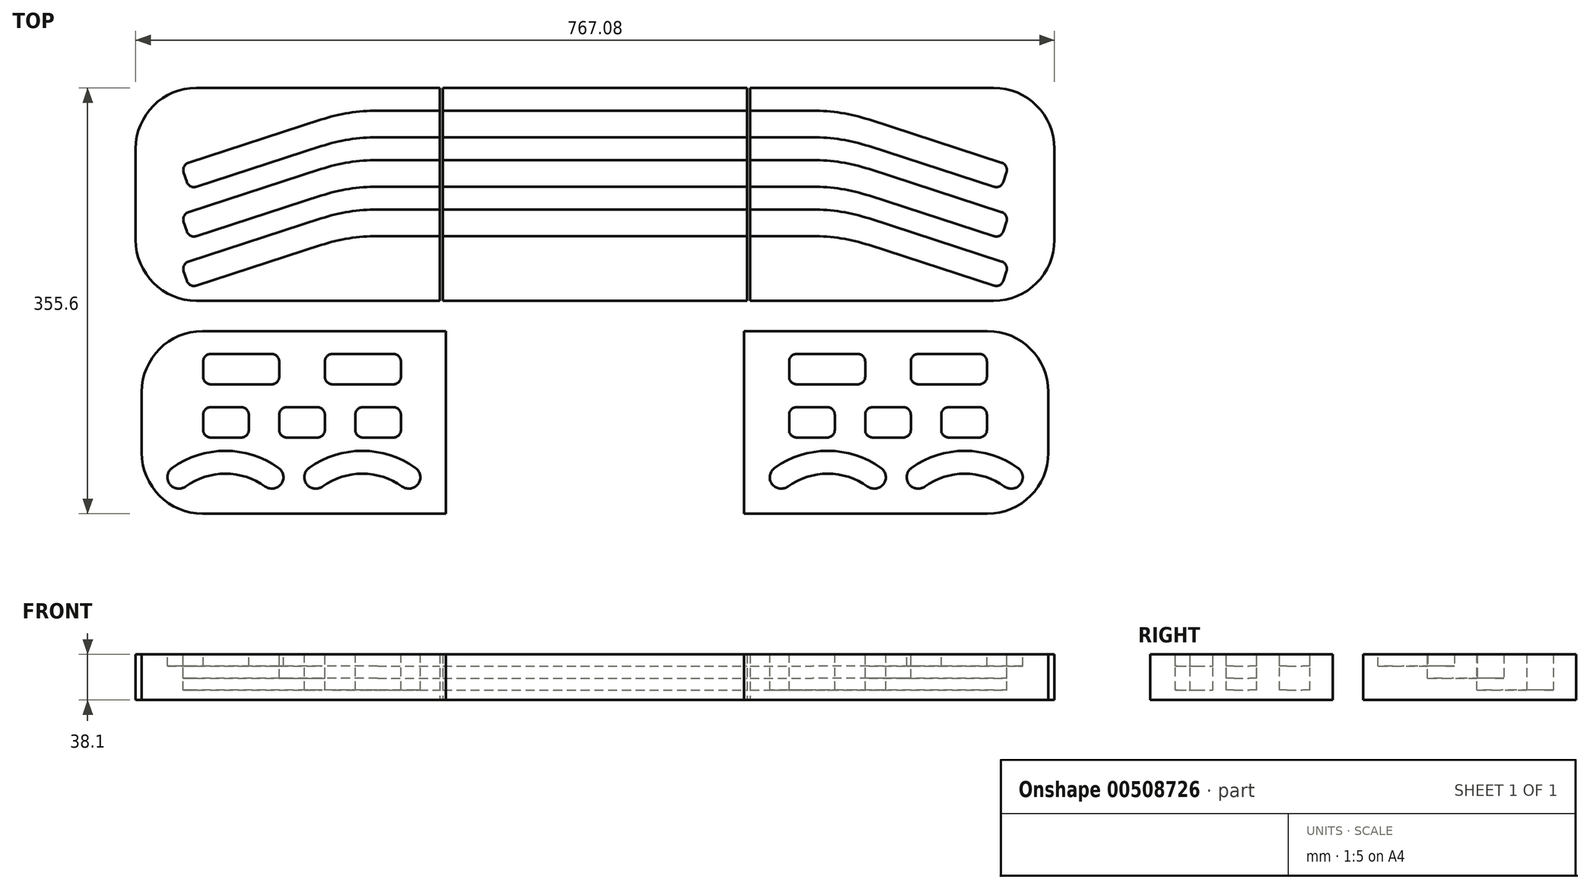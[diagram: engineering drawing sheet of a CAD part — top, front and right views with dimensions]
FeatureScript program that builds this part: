
annotation { "Feature Type Name" : "Feature", "Feature Type Description" : "" }
export const myFeature = defineFeature(function(context is Context, id is Id, definition is map)
    precondition{}
    {
        {
            var Q0;
            Q0=qCreatedBy(makeId("Top.planeOp"),FACE);
            var sketch = newSketch(context, id + "F0", { "sketchPlane" : qUnion([Q0])});
            skLineSegment(sketch, "E0.bottom", {"start": v(-716.28, 177.8) * mm, "end": v(-513.08, 177.8) * mm});
            skLineSegment(sketch, "E0.top", {"start": v(-716.28, 0) * mm, "end": v(-513.08, 0) * mm});
            skLineSegment(sketch, "E0.left", {"start": v(-767.08, 127) * mm, "end": v(-767.08, 50.8) * mm});
            skLineSegment(sketch, "E0.right", {"start": v(0, 127) * mm, "end": v(0, 50.8) * mm});
            skPoint(sketch, "E1.visualSharp", {"position": v(-767.08, 177.8) * mm});
            skArc(sketch, "E1.filletArc", {"start": v(-716.28, 177.8) * mm, "mid": v(-752.2, 162.92) * mm, "end": v(-767.08, 127) * mm});
            skPoint(sketch, "E2.visualSharp", {"position": v(0, 177.8) * mm});
            skArc(sketch, "E2.filletArc", {"start": v(0, 127) * mm, "mid": v(-14.88, 162.92) * mm, "end": v(-50.8, 177.8) * mm});
            skPoint(sketch, "E3.visualSharp", {"position": v(0, 0) * mm});
            skArc(sketch, "E3.filletArc", {"start": v(-50.8, 0) * mm, "mid": v(-14.88, 14.88) * mm, "end": v(0, 50.8) * mm});
            skPoint(sketch, "E4.visualSharp", {"position": v(-767.08, 0) * mm});
            skArc(sketch, "E4.filletArc", {"start": v(-767.08, 50.8) * mm, "mid": v(-752.2, 14.88) * mm, "end": v(-716.28, 0) * mm});
            skLineSegment(sketch, "E5", {"start": v(-513.08, 177.8) * mm, "end": v(-513.08, 0) * mm});
            skLineSegment(sketch, "E6", {"start": v(-254, 177.8) * mm, "end": v(-254, 0) * mm});
            skLineSegment(sketch, "E7", {"start": v(-510.54, 177.8) * mm, "end": v(-510.54, 0) * mm});
            skLineSegment(sketch, "E8", {"start": v(-256.54, 177.8) * mm, "end": v(-256.54, 0) * mm});
            skLineSegment(sketch, "E9.trimOffspring", {"start": v(-254, 177.8) * mm, "end": v(-50.8, 177.8) * mm});
            skLineSegment(sketch, "E10.trimOffspring", {"start": v(-254, 0) * mm, "end": v(-50.8, 0) * mm});
            skLineSegment(sketch, "E11.trimOffspring", {"start": v(-510.54, 177.8) * mm, "end": v(-256.54, 177.8) * mm});
            skLineSegment(sketch, "E12.trimOffspring", {"start": v(-510.54, 0) * mm, "end": v(-256.54, 0) * mm});
            skSolve(sketch);
        }
        {
            var Q0;
            Q0=makeQuery(id+"F0.imprint","IMPRINT",FACE,{"disambiguationData":[TD([[makeQuery(id+"F0.imprint","IMPRINT",EDGE,{"derivedFrom":sQuery(id+"F0.wireOp",EDGE,"E0.left")}),1.0]])]});
            var Q1;
            Q1=makeQuery(id+"F0.imprint","IMPRINT",FACE,{"disambiguationData":[TD([[makeQuery(id+"F0.imprint","IMPRINT",EDGE,{"derivedFrom":sQuery(id+"F0.wireOp",EDGE,"E0.right")}),-1.0]])]});
            var Q2;
            {var subQ0=sQuery(id+"F0.wireOp",EDGE,"E5");Q2=makeQuery(id+"F0.imprint","IMPRINT",FACE,{"disambiguationData":[TD([[makeQuery(id+"F0.imprint","IMPRINT",EDGE,{"derivedFrom":subQ0}),1.0]])]});}
            var Q3;
            Q3=makeQuery(id+"F0.imprint","IMPRINT",FACE,{"disambiguationData":[TD([[makeQuery(id+"F0.imprint","IMPRINT",EDGE,{"derivedFrom":sQuery(id+"F0.wireOp",EDGE,"E7")}),1.0]])]});
            extrude(context, id + "F1", {"entities" : qUnion([Q0, Q1, Q2, Q3]), "depth" : 38.1 * mm});
        }
        {
            var Q0;
            Q0=makeQuery(id+"F1.opExtrude","CAP_FACE",FACE,{"disambiguationData":[OSD([sQuery(id+"F0.wireOp",EDGE,"E0.bottom"),sQuery(id+"F0.wireOp",EDGE,"E0.top"),sQuery(id+"F0.wireOp",EDGE,"E0.left"),sQuery(id+"F0.wireOp",EDGE,"E0.right"),sQuery(id+"F0.wireOp",EDGE,"E1.filletArc"),sQuery(id+"F0.wireOp",EDGE,"E2.filletArc"),sQuery(id+"F0.wireOp",EDGE,"E3.filletArc"),sQuery(id+"F0.wireOp",EDGE,"E4.filletArc")])],"isStart":false});
            var sketch = newSketch(context, id + "F2", { "sketchPlane" : qUnion([Q0])});
            skLineSegment(sketch, "E13.bottom", {"start": v(-565.14, 158.75) * mm, "end": v(-201.94, 158.75) * mm});
            skLineSegment(sketch, "E13.top", {"start": v(-565.14, 136.53) * mm, "end": v(-201.94, 136.53) * mm});
            skLineSegment(sketch, "E14", {"start": v(-612.24, 151.3) * mm, "end": v(-722.94, 115.32) * mm});
            skLineSegment(sketch, "E15", {"start": v(-727.02, 107.32) * mm, "end": v(-724.41, 99.3) * mm});
            skLineSegment(sketch, "E16", {"start": v(-716.4, 95.22) * mm, "end": v(-612.24, 129.07) * mm});
            skLineSegment(sketch, "E17", {"start": v(-154.84, 151.3) * mm, "end": v(-44.14, 115.32) * mm});
            skLineSegment(sketch, "E18", {"start": v(-40.06, 107.32) * mm, "end": v(-42.67, 99.3) * mm});
            skLineSegment(sketch, "E19", {"start": v(-50.67, 95.22) * mm, "end": v(-154.84, 129.07) * mm});
            skPoint(sketch, "E20.visualSharp", {"position": v(-589.28, 158.75) * mm});
            skArc(sketch, "E20.filletArc", {"start": v(-565.14, 158.75) * mm, "mid": v(-588.98, 156.87) * mm, "end": v(-612.24, 151.3) * mm});
            skPoint(sketch, "E21.visualSharp", {"position": v(-589.28, 136.53) * mm});
            skArc(sketch, "E21.filletArc", {"start": v(-565.14, 136.53) * mm, "mid": v(-588.98, 134.65) * mm, "end": v(-612.24, 129.07) * mm});
            skPoint(sketch, "E22.visualSharp", {"position": v(-177.8, 158.75) * mm});
            skArc(sketch, "E22.filletArc", {"start": v(-154.84, 151.3) * mm, "mid": v(-178.1, 156.87) * mm, "end": v(-201.94, 158.75) * mm});
            skPoint(sketch, "E23.visualSharp", {"position": v(-177.8, 136.53) * mm});
            skArc(sketch, "E23.filletArc", {"start": v(-154.84, 129.07) * mm, "mid": v(-178.1, 134.65) * mm, "end": v(-201.94, 136.53) * mm});
            skPoint(sketch, "E24.visualSharp", {"position": v(-38.1, 113.36) * mm});
            skArc(sketch, "E24.filletArc", {"start": v(-40.06, 107.32) * mm, "mid": v(-40.44, 112.16) * mm, "end": v(-44.14, 115.32) * mm});
            skPoint(sketch, "E25.visualSharp", {"position": v(-44.63, 93.26) * mm});
            skArc(sketch, "E25.filletArc", {"start": v(-50.67, 95.22) * mm, "mid": v(-45.83, 95.6) * mm, "end": v(-42.67, 99.3) * mm});
            skPoint(sketch, "E26.visualSharp", {"position": v(-728.98, 113.36) * mm});
            skArc(sketch, "E26.filletArc", {"start": v(-722.94, 115.32) * mm, "mid": v(-726.64, 112.16) * mm, "end": v(-727.02, 107.32) * mm});
            skPoint(sketch, "E27.visualSharp", {"position": v(-722.45, 93.26) * mm});
            skArc(sketch, "E27.filletArc", {"start": v(-724.41, 99.3) * mm, "mid": v(-721.25, 95.6) * mm, "end": v(-716.4, 95.22) * mm});
            skLineSegment(sketch, "E28.bottom", {"start": v(-565.14, 117.47) * mm, "end": v(-201.94, 117.47) * mm});
            skLineSegment(sketch, "E28.top", {"start": v(-565.14, 95.25) * mm, "end": v(-201.94, 95.25) * mm});
            skLineSegment(sketch, "E29", {"start": v(-612.24, 110.02) * mm, "end": v(-722.94, 74.05) * mm});
            skLineSegment(sketch, "E30", {"start": v(-727.02, 66.04) * mm, "end": v(-724.41, 58.02) * mm});
            skLineSegment(sketch, "E31", {"start": v(-716.4, 53.94) * mm, "end": v(-612.24, 87.8) * mm});
            skLineSegment(sketch, "E32", {"start": v(-154.84, 110.02) * mm, "end": v(-44.14, 74.05) * mm});
            skLineSegment(sketch, "E33", {"start": v(-40.06, 66.04) * mm, "end": v(-42.67, 58.02) * mm});
            skLineSegment(sketch, "E34", {"start": v(-50.67, 53.94) * mm, "end": v(-154.84, 87.8) * mm});
            skPoint(sketch, "E35.visualSharp", {"position": v(-589.28, 117.48) * mm});
            skArc(sketch, "E35.filletArc", {"start": v(-565.14, 117.48) * mm, "mid": v(-588.98, 115.6) * mm, "end": v(-612.24, 110.02) * mm});
            skPoint(sketch, "E36.visualSharp", {"position": v(-589.28, 95.25) * mm});
            skArc(sketch, "E36.filletArc", {"start": v(-565.14, 95.25) * mm, "mid": v(-588.98, 93.37) * mm, "end": v(-612.24, 87.8) * mm});
            skPoint(sketch, "E37.visualSharp", {"position": v(-177.8, 117.48) * mm});
            skArc(sketch, "E37.filletArc", {"start": v(-154.84, 110.02) * mm, "mid": v(-178.1, 115.6) * mm, "end": v(-201.94, 117.48) * mm});
            skPoint(sketch, "E38.visualSharp", {"position": v(-177.8, 95.25) * mm});
            skArc(sketch, "E38.filletArc", {"start": v(-154.84, 87.8) * mm, "mid": v(-178.1, 93.37) * mm, "end": v(-201.94, 95.25) * mm});
            skPoint(sketch, "E39.visualSharp", {"position": v(-38.1, 72.08) * mm});
            skArc(sketch, "E39.filletArc", {"start": v(-40.06, 66.04) * mm, "mid": v(-40.44, 70.89) * mm, "end": v(-44.14, 74.05) * mm});
            skPoint(sketch, "E40.visualSharp", {"position": v(-44.63, 51.98) * mm});
            skArc(sketch, "E40.filletArc", {"start": v(-50.67, 53.94) * mm, "mid": v(-45.83, 54.32) * mm, "end": v(-42.67, 58.02) * mm});
            skPoint(sketch, "E41.visualSharp", {"position": v(-728.98, 72.08) * mm});
            skArc(sketch, "E41.filletArc", {"start": v(-722.94, 74.05) * mm, "mid": v(-726.64, 70.89) * mm, "end": v(-727.02, 66.04) * mm});
            skPoint(sketch, "E42.visualSharp", {"position": v(-722.45, 51.98) * mm});
            skArc(sketch, "E42.filletArc", {"start": v(-724.41, 58.02) * mm, "mid": v(-721.25, 54.32) * mm, "end": v(-716.4, 53.94) * mm});
            skLineSegment(sketch, "E43.bottom", {"start": v(-565.14, 76.2) * mm, "end": v(-201.94, 76.2) * mm});
            skLineSegment(sketch, "E43.top", {"start": v(-565.14, 53.97) * mm, "end": v(-201.94, 53.97) * mm});
            skLineSegment(sketch, "E44", {"start": v(-612.24, 68.74) * mm, "end": v(-722.94, 32.77) * mm});
            skLineSegment(sketch, "E45", {"start": v(-727.02, 24.77) * mm, "end": v(-724.41, 16.75) * mm});
            skLineSegment(sketch, "E46", {"start": v(-716.4, 12.67) * mm, "end": v(-612.24, 46.52) * mm});
            skLineSegment(sketch, "E47", {"start": v(-154.84, 68.74) * mm, "end": v(-44.14, 32.77) * mm});
            skLineSegment(sketch, "E48", {"start": v(-40.06, 24.77) * mm, "end": v(-42.67, 16.75) * mm});
            skLineSegment(sketch, "E49", {"start": v(-50.67, 12.67) * mm, "end": v(-154.84, 46.52) * mm});
            skPoint(sketch, "E50.visualSharp", {"position": v(-589.28, 76.2) * mm});
            skArc(sketch, "E50.filletArc", {"start": v(-565.14, 76.2) * mm, "mid": v(-588.98, 74.32) * mm, "end": v(-612.24, 68.74) * mm});
            skPoint(sketch, "E51.visualSharp", {"position": v(-589.28, 53.98) * mm});
            skArc(sketch, "E51.filletArc", {"start": v(-565.14, 53.98) * mm, "mid": v(-588.98, 52.1) * mm, "end": v(-612.24, 46.52) * mm});
            skPoint(sketch, "E52.visualSharp", {"position": v(-177.8, 76.2) * mm});
            skArc(sketch, "E52.filletArc", {"start": v(-154.84, 68.74) * mm, "mid": v(-178.1, 74.32) * mm, "end": v(-201.94, 76.2) * mm});
            skPoint(sketch, "E53.visualSharp", {"position": v(-177.8, 53.97) * mm});
            skArc(sketch, "E53.filletArc", {"start": v(-154.84, 46.52) * mm, "mid": v(-178.1, 52.1) * mm, "end": v(-201.94, 53.98) * mm});
            skPoint(sketch, "E54.visualSharp", {"position": v(-38.1, 30.8) * mm});
            skArc(sketch, "E54.filletArc", {"start": v(-40.06, 24.77) * mm, "mid": v(-40.44, 29.61) * mm, "end": v(-44.14, 32.77) * mm});
            skPoint(sketch, "E55.visualSharp", {"position": v(-44.63, 10.7) * mm});
            skArc(sketch, "E55.filletArc", {"start": v(-50.67, 12.67) * mm, "mid": v(-45.83, 13.05) * mm, "end": v(-42.67, 16.75) * mm});
            skPoint(sketch, "E56.visualSharp", {"position": v(-728.98, 30.8) * mm});
            skArc(sketch, "E56.filletArc", {"start": v(-722.94, 32.77) * mm, "mid": v(-726.64, 29.61) * mm, "end": v(-727.02, 24.77) * mm});
            skPoint(sketch, "E57.visualSharp", {"position": v(-722.45, 10.7) * mm});
            skArc(sketch, "E57.filletArc", {"start": v(-724.41, 16.75) * mm, "mid": v(-721.25, 13.05) * mm, "end": v(-716.4, 12.67) * mm});
            skLineSegment(sketch, "E58", {"start": v(-614.68, 177.8) * mm, "end": v(-614.68, 0) * mm, "construction": true});
            skSolve(sketch);
        }
        {
            var Q0;
            Q0=qCreatedBy(makeId("Top.planeOp"),FACE);
            var sketch = newSketch(context, id + "F3", { "sketchPlane" : qUnion([Q0])});
            skLineSegment(sketch, "E59.bottom", {"start": v(-711.2, -25.4) * mm, "end": v(-508, -25.4) * mm});
            skLineSegment(sketch, "E59.top", {"start": v(-711.2, -177.8) * mm, "end": v(-508, -177.8) * mm});
            skLineSegment(sketch, "E59.left", {"start": v(-762, -76.2) * mm, "end": v(-762, -127) * mm});
            skPoint(sketch, "E60.visualSharp", {"position": v(-762, -25.4) * mm});
            skArc(sketch, "E60.filletArc", {"start": v(-711.2, -25.4) * mm, "mid": v(-747.12, -40.28) * mm, "end": v(-762, -76.2) * mm});
            skPoint(sketch, "E61.visualSharp", {"position": v(0, -25.4) * mm});
            skPoint(sketch, "E62.visualSharp", {"position": v(0, -177.8) * mm});
            skPoint(sketch, "E63.visualSharp", {"position": v(-762, -177.8) * mm});
            skArc(sketch, "E63.filletArc", {"start": v(-762, -127) * mm, "mid": v(-747.12, -162.92) * mm, "end": v(-711.2, -177.8) * mm});
            skLineSegment(sketch, "E64", {"start": v(-508, -25.4) * mm, "end": v(-508, -177.8) * mm});
            skSolve(sketch);
        }
        {
            var Q0;
            Q0=makeQuery(id+"F3.imprint","IMPRINT",FACE,{"disambiguationData":[TD([[makeQuery(id+"F3.imprint","IMPRINT",EDGE,{"derivedFrom":sQuery(id+"F3.wireOp",EDGE,"E59.bottom")}),-1.0]])]});
            extrude(context, id + "F4", {"entities" : qUnion([Q0]), "depth" : 38.1 * mm});
        }
        {
            var Q0;
            Q0=makeQuery(id+"F4.opExtrude","CAP_FACE",FACE,{"disambiguationData":[OSD([sQuery(id+"F3.wireOp",EDGE,"E59.bottom"),sQuery(id+"F3.wireOp",EDGE,"E59.top"),sQuery(id+"F3.wireOp",EDGE,"E59.left"),sQuery(id+"F3.wireOp",EDGE,"E59.right"),sQuery(id+"F3.wireOp",EDGE,"E60.filletArc"),sQuery(id+"F3.wireOp",EDGE,"E61.filletArc"),sQuery(id+"F3.wireOp",EDGE,"E62.filletArc"),sQuery(id+"F3.wireOp",EDGE,"E63.filletArc")])],"isStart":false});
            var sketch = newSketch(context, id + "F5", { "sketchPlane" : qUnion([Q0])});
            skLineSegment(sketch, "E65.bottom", {"start": v(-704.32, -69.85) * mm, "end": v(-653.52, -69.85) * mm});
            skLineSegment(sketch, "E65.top", {"start": v(-704.32, -44.45) * mm, "end": v(-653.52, -44.45) * mm});
            skLineSegment(sketch, "E65.left", {"start": v(-710.67, -63.5) * mm, "end": v(-710.67, -50.8) * mm});
            skLineSegment(sketch, "E65.right", {"start": v(-647.17, -63.5) * mm, "end": v(-647.17, -50.8) * mm});
            skPoint(sketch, "E66.visualSharp", {"position": v(-710.67, -44.45) * mm});
            skArc(sketch, "E66.filletArc", {"start": v(-704.32, -44.45) * mm, "mid": v(-708.81, -46.3) * mm, "end": v(-710.67, -50.8) * mm});
            skPoint(sketch, "E67.visualSharp", {"position": v(-710.67, -69.85) * mm});
            skArc(sketch, "E67.filletArc", {"start": v(-710.67, -63.5) * mm, "mid": v(-708.81, -68) * mm, "end": v(-704.32, -69.85) * mm});
            skPoint(sketch, "E68.visualSharp", {"position": v(-647.17, -44.45) * mm});
            skArc(sketch, "E68.filletArc", {"start": v(-647.17, -50.8) * mm, "mid": v(-649.03, -46.3) * mm, "end": v(-653.52, -44.45) * mm});
            skPoint(sketch, "E69.visualSharp", {"position": v(-647.17, -69.85) * mm});
            skArc(sketch, "E69.filletArc", {"start": v(-653.52, -69.85) * mm, "mid": v(-649.03, -68) * mm, "end": v(-647.17, -63.5) * mm});
            skLineSegment(sketch, "E70.bottom", {"start": v(-602.72, -69.85) * mm, "end": v(-551.92, -69.85) * mm});
            skLineSegment(sketch, "E70.top", {"start": v(-602.72, -44.45) * mm, "end": v(-551.92, -44.45) * mm});
            skLineSegment(sketch, "E70.left", {"start": v(-609.07, -63.5) * mm, "end": v(-609.07, -50.8) * mm});
            skLineSegment(sketch, "E70.right", {"start": v(-545.57, -63.5) * mm, "end": v(-545.57, -50.8) * mm});
            skPoint(sketch, "E71.visualSharp", {"position": v(-609.07, -44.45) * mm});
            skArc(sketch, "E71.filletArc", {"start": v(-602.72, -44.45) * mm, "mid": v(-607.21, -46.3) * mm, "end": v(-609.07, -50.8) * mm});
            skPoint(sketch, "E72.visualSharp", {"position": v(-609.07, -69.85) * mm});
            skArc(sketch, "E72.filletArc", {"start": v(-609.07, -63.5) * mm, "mid": v(-607.21, -68) * mm, "end": v(-602.72, -69.85) * mm});
            skPoint(sketch, "E73.visualSharp", {"position": v(-545.57, -44.45) * mm});
            skArc(sketch, "E73.filletArc", {"start": v(-545.57, -50.8) * mm, "mid": v(-547.43, -46.3) * mm, "end": v(-551.92, -44.45) * mm});
            skPoint(sketch, "E74.visualSharp", {"position": v(-545.57, -69.85) * mm});
            skArc(sketch, "E74.filletArc", {"start": v(-551.92, -69.85) * mm, "mid": v(-547.43, -68) * mm, "end": v(-545.57, -63.5) * mm});
            skLineSegment(sketch, "E75.bottom", {"start": v(-704.32, -114.3) * mm, "end": v(-678.92, -114.3) * mm});
            skLineSegment(sketch, "E75.top", {"start": v(-704.32, -88.9) * mm, "end": v(-678.92, -88.9) * mm});
            skLineSegment(sketch, "E75.left", {"start": v(-710.67, -107.95) * mm, "end": v(-710.67, -95.25) * mm});
            skLineSegment(sketch, "E75.right", {"start": v(-672.57, -107.95) * mm, "end": v(-672.57, -95.25) * mm});
            skPoint(sketch, "E76.visualSharp", {"position": v(-710.67, -88.9) * mm});
            skArc(sketch, "E76.filletArc", {"start": v(-704.32, -88.9) * mm, "mid": v(-708.81, -90.76) * mm, "end": v(-710.67, -95.25) * mm});
            skPoint(sketch, "E77.visualSharp", {"position": v(-710.67, -114.3) * mm});
            skArc(sketch, "E77.filletArc", {"start": v(-710.67, -107.95) * mm, "mid": v(-708.81, -112.44) * mm, "end": v(-704.32, -114.3) * mm});
            skPoint(sketch, "E78.visualSharp", {"position": v(-672.57, -88.9) * mm});
            skArc(sketch, "E78.filletArc", {"start": v(-672.57, -95.25) * mm, "mid": v(-674.43, -90.76) * mm, "end": v(-678.92, -88.9) * mm});
            skPoint(sketch, "E79.visualSharp", {"position": v(-672.57, -114.3) * mm});
            skArc(sketch, "E79.filletArc", {"start": v(-678.92, -114.3) * mm, "mid": v(-674.43, -112.44) * mm, "end": v(-672.57, -107.95) * mm});
            skLineSegment(sketch, "E80.bottom", {"start": v(-640.82, -114.3) * mm, "end": v(-615.42, -114.3) * mm});
            skLineSegment(sketch, "E80.top", {"start": v(-640.82, -88.9) * mm, "end": v(-615.42, -88.9) * mm});
            skLineSegment(sketch, "E80.left", {"start": v(-647.17, -107.95) * mm, "end": v(-647.17, -95.25) * mm});
            skLineSegment(sketch, "E80.right", {"start": v(-609.07, -107.95) * mm, "end": v(-609.07, -95.25) * mm});
            skPoint(sketch, "E81.visualSharp", {"position": v(-647.17, -88.9) * mm});
            skArc(sketch, "E81.filletArc", {"start": v(-640.82, -88.9) * mm, "mid": v(-645.31, -90.76) * mm, "end": v(-647.17, -95.25) * mm});
            skPoint(sketch, "E82.visualSharp", {"position": v(-647.17, -114.3) * mm});
            skArc(sketch, "E82.filletArc", {"start": v(-647.17, -107.95) * mm, "mid": v(-645.31, -112.44) * mm, "end": v(-640.82, -114.3) * mm});
            skPoint(sketch, "E83.visualSharp", {"position": v(-609.07, -88.9) * mm});
            skArc(sketch, "E83.filletArc", {"start": v(-609.07, -95.25) * mm, "mid": v(-610.93, -90.76) * mm, "end": v(-615.42, -88.9) * mm});
            skPoint(sketch, "E84.visualSharp", {"position": v(-609.07, -114.3) * mm});
            skArc(sketch, "E84.filletArc", {"start": v(-615.42, -114.3) * mm, "mid": v(-610.93, -112.44) * mm, "end": v(-609.07, -107.95) * mm});
            skLineSegment(sketch, "E85.bottom", {"start": v(-577.32, -114.3) * mm, "end": v(-551.92, -114.3) * mm});
            skLineSegment(sketch, "E85.top", {"start": v(-577.32, -88.9) * mm, "end": v(-551.92, -88.9) * mm});
            skLineSegment(sketch, "E85.left", {"start": v(-583.67, -107.95) * mm, "end": v(-583.67, -95.25) * mm});
            skLineSegment(sketch, "E85.right", {"start": v(-545.57, -107.95) * mm, "end": v(-545.57, -95.25) * mm});
            skPoint(sketch, "E86.visualSharp", {"position": v(-583.67, -88.9) * mm});
            skArc(sketch, "E86.filletArc", {"start": v(-577.32, -88.9) * mm, "mid": v(-581.81, -90.76) * mm, "end": v(-583.67, -95.25) * mm});
            skPoint(sketch, "E87.visualSharp", {"position": v(-583.67, -114.3) * mm});
            skArc(sketch, "E87.filletArc", {"start": v(-583.67, -107.95) * mm, "mid": v(-581.81, -112.44) * mm, "end": v(-577.32, -114.3) * mm});
            skPoint(sketch, "E88.visualSharp", {"position": v(-545.57, -88.9) * mm});
            skArc(sketch, "E88.filletArc", {"start": v(-545.57, -95.25) * mm, "mid": v(-547.43, -90.76) * mm, "end": v(-551.92, -88.9) * mm});
            skPoint(sketch, "E89.visualSharp", {"position": v(-545.57, -114.3) * mm});
            skArc(sketch, "E89.filletArc", {"start": v(-551.92, -114.3) * mm, "mid": v(-547.43, -112.44) * mm, "end": v(-545.57, -107.95) * mm});
            skLineSegment(sketch, "E90", {"start": v(-736.6, -139.7) * mm, "end": v(-647.7, -139.7) * mm, "construction": true});
            skArc(sketch, "E91", {"start": v(-647.7, -139.7) * mm, "mid": v(-692.15, -125.4) * mm, "end": v(-736.6, -139.7) * mm});
            skArc(sketch, "E92.0", {"start": v(-658.81, -155.17) * mm, "mid": v(-692.15, -144.44) * mm, "end": v(-725.49, -155.17) * mm});
            skArc(sketch, "E93", {"start": v(-658.81, -155.17) * mm, "mid": v(-645.52, -153) * mm, "end": v(-647.7, -139.7) * mm});
            skArc(sketch, "E94", {"start": v(-736.6, -139.7) * mm, "mid": v(-738.78, -153) * mm, "end": v(-725.49, -155.17) * mm});
            skLineSegment(sketch, "E95", {"start": v(-622.3, -139.7) * mm, "end": v(-533.4, -139.7) * mm, "construction": true});
            skArc(sketch, "E96", {"start": v(-533.4, -139.7) * mm, "mid": v(-577.85, -125.4) * mm, "end": v(-622.3, -139.7) * mm});
            skArc(sketch, "E97.0", {"start": v(-544.51, -155.17) * mm, "mid": v(-577.85, -144.44) * mm, "end": v(-611.19, -155.17) * mm});
            skArc(sketch, "E98", {"start": v(-544.51, -155.17) * mm, "mid": v(-531.22, -153) * mm, "end": v(-533.4, -139.7) * mm});
            skArc(sketch, "E99", {"start": v(-622.3, -139.7) * mm, "mid": v(-624.48, -153) * mm, "end": v(-611.19, -155.17) * mm});
            skSolve(sketch);
        }
        {
            var Q0;
            Q0=makeQuery(id+"F2.imprint","IMPRINT",FACE,{"disambiguationData":[TD([[makeQuery(id+"F2.imprint","IMPRINT",EDGE,{"derivedFrom":sQuery(id+"F2.wireOp",EDGE,"E13.bottom")}),-1.0]])]});
            var Q1;
            Q1=makeQuery(id+"F2.imprint","IMPRINT",FACE,{"disambiguationData":[TD([[makeQuery(id+"F2.imprint","IMPRINT",EDGE,{"derivedFrom":sQuery(id+"F2.wireOp",EDGE,"b87c750a-75f9-4460-9ffb-316df826d532.bottom")}),-1.0]])]});
            var Q2;
            Q2=makeQuery(id+"F2.imprint","IMPRINT",FACE,{"disambiguationData":[TD([[makeQuery(id+"F2.imprint","IMPRINT",EDGE,{"derivedFrom":sQuery(id+"F2.wireOp",EDGE,"yCTn19MA-GANU-wBFY-IAiZ-1ZZAkRyIm9CM.bottom")}),-1.0]])]});
            var Q3;
            Q3=makeQuery(id+"F2.imprint","IMPRINT",FACE,{"disambiguationData":[TD([[makeQuery(id+"F2.imprint","IMPRINT",EDGE,{"derivedFrom":sQuery(id+"F2.wireOp",EDGE,"gyKfe8PN-7yOE-q1RT-Tw1c-nsYPelPwIu4A")}),1.0]])]});
            var Q4;
            Q4=makeQuery(id+"F2.imprint","IMPRINT",FACE,{"disambiguationData":[TD([[makeQuery(id+"F2.imprint","IMPRINT",EDGE,{"derivedFrom":sQuery(id+"F2.wireOp",EDGE,"aef82ebb-8d8c-4497-a7f1-0d8c1fc233172.MirrorCS")}),-1.0]])]});
            var Q5;
            Q5=makeQuery(id+"F2.imprint","IMPRINT",FACE,{"disambiguationData":[TD([[makeQuery(id+"F2.imprint","IMPRINT",EDGE,{"derivedFrom":sQuery(id+"F2.wireOp",EDGE,"aef82ebb-8d8c-4497-a7f1-0d8c1fc233171.MirrorCS")}),1.0]])]});
            var Q6;
            Q6=makeQuery(id+"F2.imprint","IMPRINT",FACE,{"disambiguationData":[TD([[makeQuery(id+"F2.imprint","IMPRINT",EDGE,{"derivedFrom":sQuery(id+"F2.wireOp",EDGE,"ad528eb3-88f2-4bc8-9327-312053784d4c7.MirrorCS")}),-1.0]])]});
            var Q7;
            Q7=makeQuery(id+"F5.imprint","IMPRINT",FACE,{"disambiguationData":[TD([[makeQuery(id+"F5.imprint","IMPRINT",EDGE,{"derivedFrom":sQuery(id+"F5.wireOp",EDGE,"E85.bottom")}),1.0]])]});
            var Q8;
            Q8=makeQuery(id+"F5.imprint","IMPRINT",FACE,{"disambiguationData":[TD([[makeQuery(id+"F5.imprint","IMPRINT",EDGE,{"derivedFrom":sQuery(id+"F5.wireOp",EDGE,"E96")}),1.0]])]});
            var Q9;
            Q9=makeQuery(id+"F5.imprint","IMPRINT",FACE,{"disambiguationData":[TD([[makeQuery(id+"F5.imprint","IMPRINT",EDGE,{"derivedFrom":sQuery(id+"F5.wireOp",EDGE,"E70.bottom")}),1.0]])]});
            extrude(context, id + "F6", {"entities" : qUnion([Q0, Q1, Q2, Q3, Q4, Q5, Q6, Q7, Q8, Q9]), "operationType" : NewBodyOperationType.REMOVE, "oppositeDirection" : true, "depth" : 30 * mm});
        }
        {
            var Q0;
            Q0=makeQuery(id+"F2.imprint","IMPRINT",FACE,{"disambiguationData":[TD([[makeQuery(id+"F2.imprint","IMPRINT",EDGE,{"derivedFrom":sQuery(id+"F2.wireOp",EDGE,"E28.bottom")}),-1.0]])]});
            var Q1;
            Q1=makeQuery(id+"F2.imprint","IMPRINT",FACE,{"disambiguationData":[TD([[makeQuery(id+"F2.imprint","IMPRINT",EDGE,{"derivedFrom":sQuery(id+"F2.wireOp",EDGE,"41bf9ecd-17d9-4c9e-8e28-f218d3024768.bottom")}),-1.0]])]});
            var Q2;
            Q2=makeQuery(id+"F2.imprint","IMPRINT",FACE,{"disambiguationData":[TD([[makeQuery(id+"F2.imprint","IMPRINT",EDGE,{"derivedFrom":sQuery(id+"F2.wireOp",EDGE,"fc10a4cb-4094-4a62-b5a6-7a231f4fa7ac.bottom")}),-1.0]])]});
            var Q3;
            Q3=makeQuery(id+"F2.imprint","IMPRINT",FACE,{"disambiguationData":[TD([[makeQuery(id+"F2.imprint","IMPRINT",EDGE,{"derivedFrom":sQuery(id+"F2.wireOp",EDGE,"EthtA0p1-tM0X-loMH-y7L1-lynVyTJc18ui")}),-1.0]])]});
            var Q4;
            Q4=makeQuery(id+"F2.imprint","IMPRINT",FACE,{"disambiguationData":[TD([[makeQuery(id+"F2.imprint","IMPRINT",EDGE,{"derivedFrom":sQuery(id+"F2.wireOp",EDGE,"aef82ebb-8d8c-4497-a7f1-0d8c1fc233175.MirrorCS")}),1.0]])]});
            var Q5;
            Q5=makeQuery(id+"F2.imprint","IMPRINT",FACE,{"disambiguationData":[TD([[makeQuery(id+"F2.imprint","IMPRINT",EDGE,{"derivedFrom":sQuery(id+"F2.wireOp",EDGE,"aef82ebb-8d8c-4497-a7f1-0d8c1fc233173.MirrorCS")}),-1.0]])]});
            var Q6;
            Q6=makeQuery(id+"F2.imprint","IMPRINT",FACE,{"disambiguationData":[TD([[makeQuery(id+"F2.imprint","IMPRINT",EDGE,{"derivedFrom":sQuery(id+"F2.wireOp",EDGE,"ad528eb3-88f2-4bc8-9327-312053784d4c0.MirrorCS")}),-1.0]])]});
            var Q7;
            Q7=makeQuery(id+"F5.imprint","IMPRINT",FACE,{"disambiguationData":[TD([[makeQuery(id+"F5.imprint","IMPRINT",EDGE,{"derivedFrom":sQuery(id+"F5.wireOp",EDGE,"E80.bottom")}),1.0]])]});
            extrude(context, id + "F7", {"entities" : qUnion([Q0, Q1, Q2, Q3, Q4, Q5, Q6, Q7]), "operationType" : NewBodyOperationType.REMOVE, "oppositeDirection" : true, "depth" : 20 * mm});
        }
        {
            var Q0;
            Q0=makeQuery(id+"F2.imprint","IMPRINT",FACE,{"disambiguationData":[TD([[makeQuery(id+"F2.imprint","IMPRINT",EDGE,{"derivedFrom":sQuery(id+"F2.wireOp",EDGE,"E43.bottom")}),-1.0]])]});
            var Q1;
            Q1=makeQuery(id+"F2.imprint","IMPRINT",FACE,{"disambiguationData":[TD([[makeQuery(id+"F2.imprint","IMPRINT",EDGE,{"derivedFrom":sQuery(id+"F2.wireOp",EDGE,"368ec0e7-311f-46c7-b090-769c8b22c586.bottom")}),-1.0]])]});
            var Q2;
            Q2=makeQuery(id+"F2.imprint","IMPRINT",FACE,{"disambiguationData":[TD([[makeQuery(id+"F2.imprint","IMPRINT",EDGE,{"derivedFrom":sQuery(id+"F2.wireOp",EDGE,"4f59e6f1-50b1-4c02-a2c9-0f445d1fe5a9")}),1.0]])]});
            var Q3;
            Q3=makeQuery(id+"F2.imprint","IMPRINT",FACE,{"disambiguationData":[TD([[makeQuery(id+"F2.imprint","IMPRINT",EDGE,{"derivedFrom":sQuery(id+"F2.wireOp",EDGE,"aef82ebb-8d8c-4497-a7f1-0d8c1fc233174.MirrorCS")}),-1.0]])]});
            var Q4;
            Q4=makeQuery(id+"F2.imprint","IMPRINT",FACE,{"disambiguationData":[TD([[makeQuery(id+"F2.imprint","IMPRINT",EDGE,{"derivedFrom":sQuery(id+"F2.wireOp",EDGE,"aef82ebb-8d8c-4497-a7f1-0d8c1fc2331737.MirrorCS")}),-1.0]])]});
            var Q5;
            Q5=makeQuery(id+"F5.imprint","IMPRINT",FACE,{"disambiguationData":[TD([[makeQuery(id+"F5.imprint","IMPRINT",EDGE,{"derivedFrom":sQuery(id+"F5.wireOp",EDGE,"E65.bottom")}),1.0]])]});
            var Q6;
            Q6=makeQuery(id+"F5.imprint","IMPRINT",FACE,{"disambiguationData":[TD([[makeQuery(id+"F5.imprint","IMPRINT",EDGE,{"derivedFrom":sQuery(id+"F5.wireOp",EDGE,"E75.bottom")}),1.0]])]});
            var Q7;
            Q7=makeQuery(id+"F5.imprint","IMPRINT",FACE,{"disambiguationData":[TD([[makeQuery(id+"F5.imprint","IMPRINT",EDGE,{"derivedFrom":sQuery(id+"F5.wireOp",EDGE,"E91")}),1.0]])]});
            extrude(context, id + "F8", {"entities" : qUnion([Q0, Q1, Q2, Q3, Q4, Q5, Q6, Q7]), "operationType" : NewBodyOperationType.REMOVE, "oppositeDirection" : true, "depth" : 10 * mm});
        }
        {
            var Q0;
            {var subQ0=sQuery(id+"F2.wireOp",EDGE,"E28.bottom");Q0=makeQuery(id+"F7.boolean.opBoolean","COPY",EDGE,{"disambiguationData":[topologyDisambiguationEdgeConnected([makeQuery(id+"F1.opExtrude","CAP_FACE",FACE,{"disambiguationData":[OSD([sQuery(id+"F0.wireOp",EDGE,"E7"),sQuery(id+"F0.wireOp",EDGE,"E8"),sQuery(id+"F0.wireOp",EDGE,"E11.trimOffspring"),sQuery(id+"F0.wireOp",EDGE,"E12.trimOffspring")])],"isStart":false})])],"derivedFrom":makeQuery(id+"F7.opExtrude","CAP_EDGE",EDGE,{"disambiguationData":[OSD([subQ0])],"isStart":true})});}
            cPlane(context, id + "F9", {"entities" : qUnion([Q0]), "cplaneType" : CPlaneType.MID_PLANE, "offset" : 25.4 * mm, "width" : 152.4 * mm, "height" : 152.4 * mm});
        }
        {
            var Q0;
            Q0=makeQuery(id+"F4.opExtrude","SWEPT_BODY",BODY,{"disambiguationData":[OSD([sQuery(id+"F3.wireOp",EDGE,"E59.bottom"),sQuery(id+"F3.wireOp",EDGE,"E59.top"),sQuery(id+"F3.wireOp",EDGE,"E59.left"),sQuery(id+"F3.wireOp",EDGE,"E60.filletArc"),sQuery(id+"F3.wireOp",EDGE,"E63.filletArc"),sQuery(id+"F3.wireOp",EDGE,"E64")])]});
            var Q1;
            Q1=qCreatedBy(id+"F9.planeOp",FACE);
            mirror(context, id + "F10", {"entities" : qUnion([Q0]), "mirrorPlane" : qUnion([Q1])});
        }
    });
